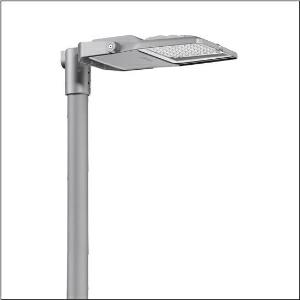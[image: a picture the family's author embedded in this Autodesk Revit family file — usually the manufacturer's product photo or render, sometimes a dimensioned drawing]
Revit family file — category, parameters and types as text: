
# Revit family: floodlight_fl_21_iq_mini___pl33t_5xa7771d4f3a_dbd7
name_source: partatom
category: Lighting Fixtures
units: mm (PartAtom-declared; Revit-internal decimal feet)

## family parameters
Cut with Voids When Loaded = No
Host = Face
Light Source = No
Part Type = Normal
Room Calculation Point = No
Round Connector Dimension = Use Diameter
Shared = No

## types (1)
- --- (1 x LED, 18390 lm, 143 W, 4000K)
    Apparent Load = 143 VA
    CIE Flux Codes = 26 75 99 100 100
    Color Rendering = 70
    Color Temperature = 4000K
    Default Elevation = 1800 mm
    Description = Floodlight FL 21 iQ mini, floodlight, primary light control with lens, of PMMA, primary optical cover: protective disc, of toughened safety glass, transparent, light distribution: PL33T, light emission: direct distribution, installation type: surface-mounted, LED, High Power LED, rated luminous flux: 18.390lm, luminous efficacy: 129lm/W, light colour: 740, colour temperature: 4000K, control: Auto-Match, Temp-Guard, Lumen-Switch, Night-Set, Smart-Wire, Light-Fading, Desk-Remote (wireless, voltage-free reading and setting of iQ features in the workshop via application-optimized NFC function/RFID function), optimised constant luminous flux control (CLO 2.0), with terminal, 6-pole, mains connection: 220..240V, AC, 50/60Hz, start of lifetime: 143W, end of service life: 152W, reduction: 61W, luminaire housing, of diecast aluminium, powder-coated, Siteco® metallic grey (DB 702S), corrosivity category C5 mid according to DIN EN ISO 12944, sealing non-destructively replaceable, please order mast flange separately, mast bracket, of steel, galvanised, powder-coated, Siteco® metallic grey (DB 702S), protection rating (complete): IP66, insulation class (complete): insulation class II (safety insulation), certification: CE, ENEC, VDE, protection symbol: D, impact resistance: IK08, permissible operating ambient temperature: -40..+40°C, permissible operating ambient temperature for outdoor applications: -40..+50°C, standard: DIN EN 12944, LABS conformity tested according to VDMA 24364:2018-05, packaging unit: 1 piece

Light Distribution: PL33T
    Height = 70 mm
    Lamp = 1 x LED
    Lamp Light Flux = 18390 lm
    Lamp Power = 143 W
    Lamp count = 1
    Length = 485 mm
    Luminous efficacy = 129 lm/W
    Manufacturer = Siteco
    ModVariant = No
    Model = 5XA7771D4F3A
    Number of Poles = 1
    OnlyDefault = Yes
    Power Factor = 1
    Product Name = Floodlight FL 21 iQ mini | PL33T
    Product group = floodlight | pylon annexe
    ProductGroupID = 6200
    Protection Class = Protection class II
    Protection Degree = IP 66
    RLX_Detail_Level = 1
    RLX_Emergency_Light_Flux = 0 lm
    RLX_Emergency_Type = 0
    RLX_Emergency_Type_DB = No
    RlxData = <blob elided: 101549 chars, md5=5b8f7895>
    Socket = socket
    Standby Power = 0 W
    System Light Flux = 18390 lm
    System Power = 143 W
    Type Comments = factory setting: luminous flux: 100 % | dim-lin: 254 | 730 mA
    Type Image = l_1007125.jpg
    URL = http://relux.com
    VarID = @adj_099241
    Voltage = 0 V
    Weight = 0.00 kg
    Width = 337 mm

## geometry (parser evidence)
native form markers: Blend x4, Sweep x13
no freeform markers — native parametric forms only
